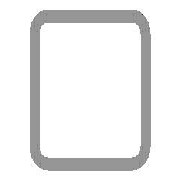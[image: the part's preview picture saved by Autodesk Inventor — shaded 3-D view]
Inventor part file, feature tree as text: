
AUTODESK INVENTOR PART (.ipt)
format: ipt  version: 2025.3 (Build 293356030, 356C)  size: 142,848 bytes
history: native  units: mm (DEFAULTED — no unit token found)
features: other x4, plane x2, split x1, sketch x1
ambient origin geometry x8: Origin, YZ Plane, XZ Plane, XY Plane, X Axis, Y Axis, Z Axis, Center Point
bodies: Solid1 (feature_tree), Body (feature_tree)
feature tree (8):
  parser-record x1  (decoder bookkeeping rows leaked as tree rows — omitted from the tree; the rows remain in map.json)
  other  "Driven Length"
  other  "Start Plane"
  other  "End Plane"
  plane  "Work Plane4"
  split  "Split1"
  sketch  "Sketch3"  dims[d3=2559.340203mm d4=0.0mm d7=6.0mm d9=80.0mm d11=80.0mm d12=3.0mm d13=160.659797mm d14=2720.0mm d15=40.0mm d16=40.0mm d17=90.0deg d18=2559.340203mm]
  plane  "Work Plane3"
